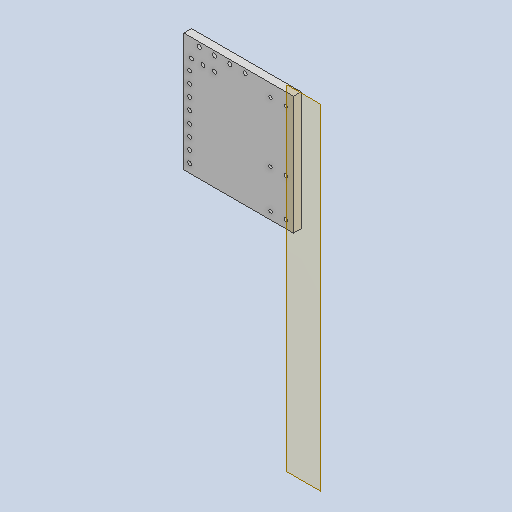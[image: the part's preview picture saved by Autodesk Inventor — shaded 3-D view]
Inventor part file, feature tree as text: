
AUTODESK INVENTOR PART (.ipt)
format: ipt  version: 2022 (Build 260153000, 153)  size: 168,448 bytes
history: native  units: in
note: dims shown in document units (in); Inventor stores cm internally (conversion verified against a paired STEP export)
features: other x6, sketch x3, extrude x2, reference x2, plane x1
ambient origin geometry x8: Origin, YZ Plane, XZ Plane, XY Plane, X Axis, Y Axis, Z Axis, Center Point
bodies: Solid1 (feature_tree)
feature tree (14):
  other  "backboard.ipt"
  extrude  "Extrusion1"  Depth=0.3937in TaperAngle=0.0deg
  extrude  "Extrusion2"  Depth=0.1693in
  other  "Solid1::backboard.ipt"
  other  "TaggingFeature1"
  sketch  "Sketch1"  dims[d0=0.3937in d1=2.1614in d2=0.0in]
  plane  "Work Plane1"
  sketch  "Sketch2"  dims[d3=0.1693in d4=0.1693in]
  reference  "Reference1"
  sketch  "Sketch3"  dims[d5=0.3937in d6=0.0in d7=0.0in d8=1.9685in d10=0.5906in d11=0.3937in d13=0.3937in]
  reference  "Reference2"
  other  "Linear Rail Assembly.iam"
  other  "backboard:1"
  other  "Lower Support_MIR:1"
